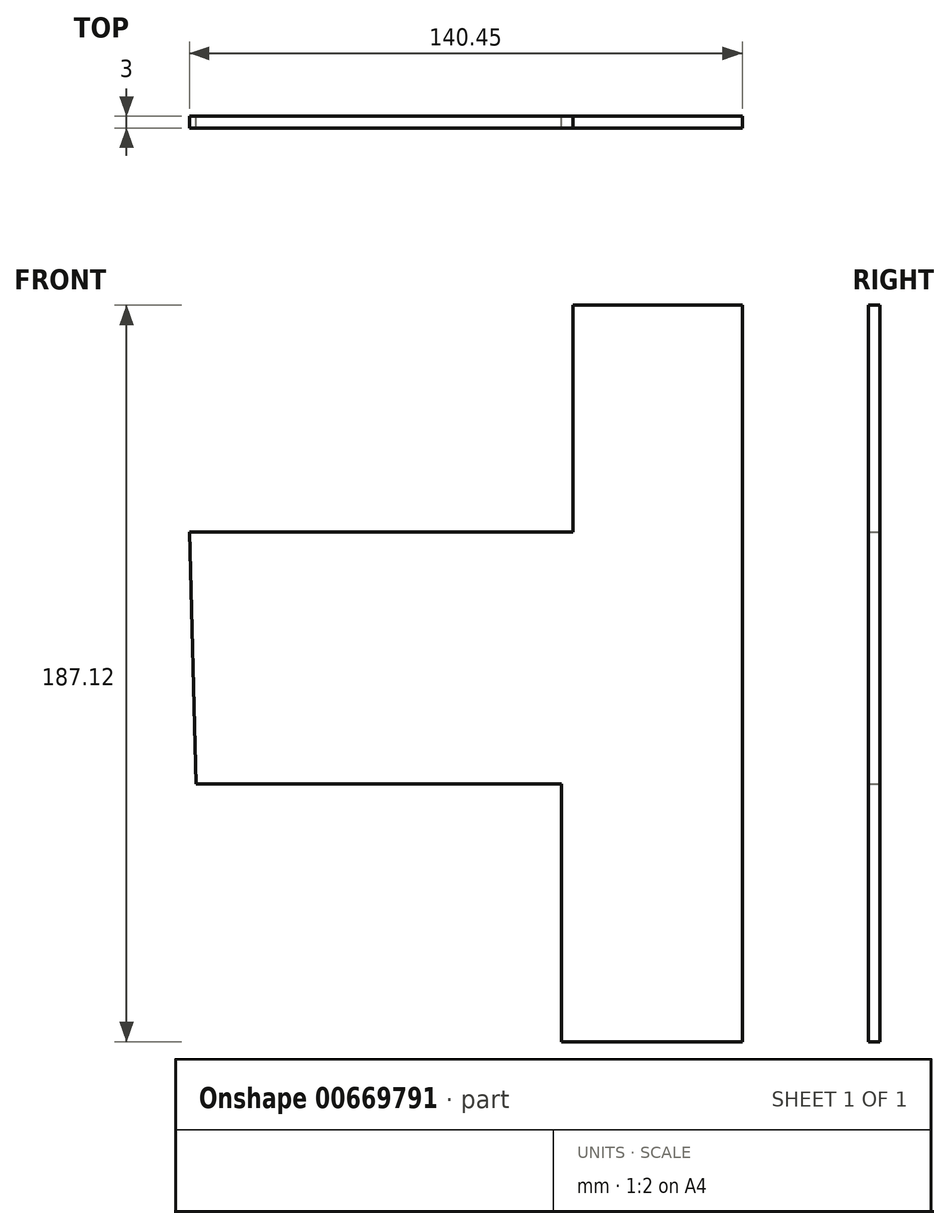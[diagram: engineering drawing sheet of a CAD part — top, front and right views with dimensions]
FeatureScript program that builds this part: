
annotation { "Feature Type Name" : "Feature", "Feature Type Description" : "" }
export const myFeature = defineFeature(function(context is Context, id is Id, definition is map)
    precondition{}
    {
        {
            var Q0;
            Q0=qCreatedBy(makeId("Front.planeOp"),FACE);
            var sketch = newSketch(context, id + "F0", { "sketchPlane" : qUnion([Q0])});
            skLineSegment(sketch, "E0", {"start": v(-53.1, -34.85) * mm, "end": v(39.71, -34.85) * mm});
            skLineSegment(sketch, "E1", {"start": v(39.71, -34.85) * mm, "end": v(39.71, -100.28) * mm});
            skLineSegment(sketch, "E2", {"start": v(39.71, -100.28) * mm, "end": v(85.65, -100.28) * mm});
            skLineSegment(sketch, "E3", {"start": v(85.65, -100.28) * mm, "end": v(85.65, 86.84) * mm});
            skLineSegment(sketch, "E4", {"start": v(85.65, 86.84) * mm, "end": v(42.67, 86.84) * mm});
            skLineSegment(sketch, "E5", {"start": v(42.67, 86.84) * mm, "end": v(42.67, 29.27) * mm});
            skLineSegment(sketch, "E6", {"start": v(42.67, 29.27) * mm, "end": v(-54.8, 29.27) * mm});
            skLineSegment(sketch, "E7", {"start": v(-54.8, 29.27) * mm, "end": v(-53.1, -34.85) * mm});
            skSolve(sketch);
        }
        {
            var Q0;
            Q0=makeQuery(id+"F0.imprint","IMPRINT",FACE,{"disambiguationData":[TD([[makeQuery(id+"F0.imprint","IMPRINT",EDGE,{"derivedFrom":sQuery(id+"F0.wireOp",EDGE,"E0")}),1.0]])]});
            extrude(context, id + "F1", {"entities" : qUnion([Q0]), "depth" : 3 * mm, "offsetDistance" : 25.4 * mm});
        }
    });
